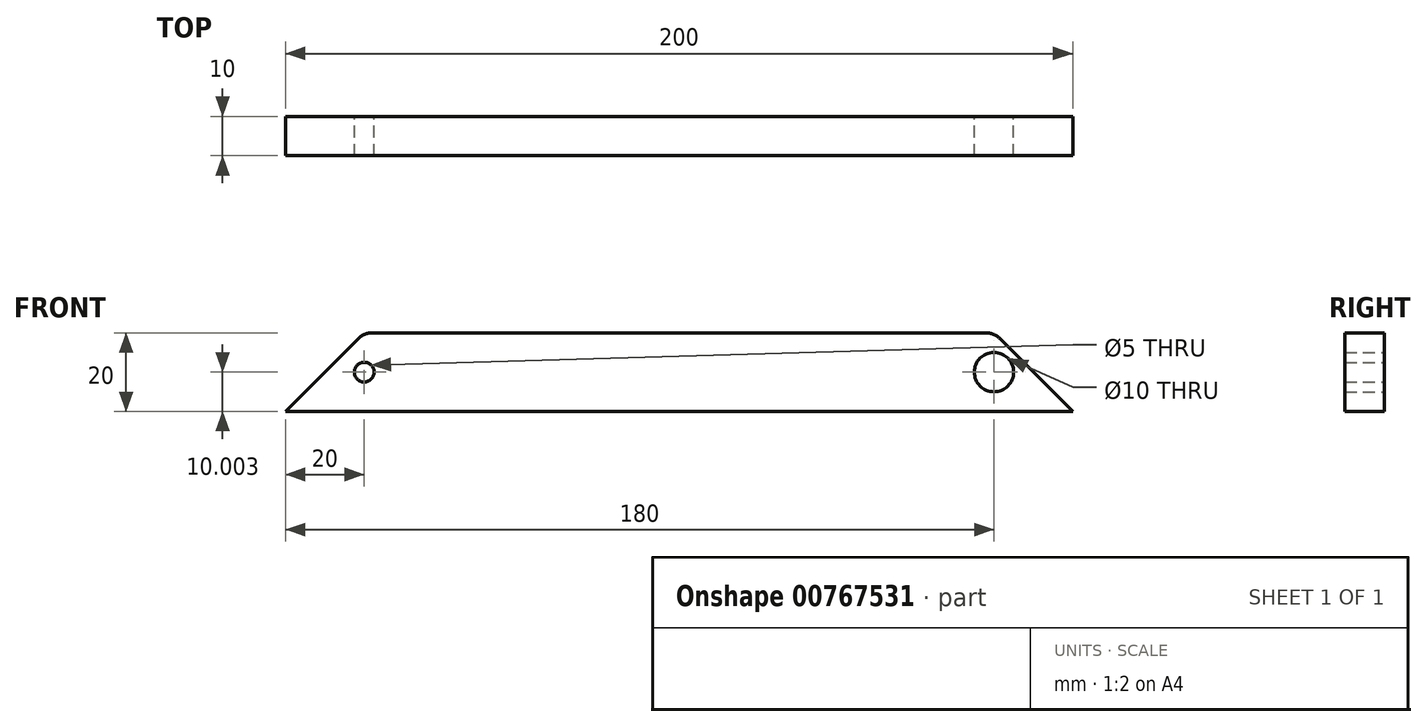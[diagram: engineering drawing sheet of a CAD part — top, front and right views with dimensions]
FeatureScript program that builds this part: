
annotation { "Feature Type Name" : "Feature", "Feature Type Description" : "" }
export const myFeature = defineFeature(function(context is Context, id is Id, definition is map)
    precondition{}
    {
        {
            var Q0;
            Q0=qCreatedBy(makeId("Front.planeOp"),FACE);
            var sketch = newSketch(context, id + "F0", { "sketchPlane" : qUnion([Q0])});
            skLineSegment(sketch, "E0.bottom", {"start": v(-75, -3.38) * mm, "end": v(125, -3.38) * mm});
            skLineSegment(sketch, "E0.top", {"start": v(-75, -23.38) * mm, "end": v(125, -23.38) * mm});
            skLineSegment(sketch, "E0.left", {"start": v(-75, -3.38) * mm, "end": v(-75, -23.38) * mm});
            skLineSegment(sketch, "E0.right", {"start": v(125, -3.38) * mm, "end": v(125, -23.38) * mm});
            skPoint(sketch, "E1", {"position": v(-55, -13.38) * mm});
            skPoint(sketch, "E2", {"position": v(105, -13.38) * mm});
            skCircle(sketch, "E3", {"center": v(-55, -13.38) * mm, "radius": 2.5 * mm});
            skCircle(sketch, "E4", {"center": v(105, -13.38) * mm, "radius": 5 * mm});
            skSolve(sketch);
        }
        {
            var Q0;
            Q0=makeQuery(id+"F0.imprint","IMPRINT",FACE,{"disambiguationData":[TD([[makeQuery(id+"F0.imprint","IMPRINT",EDGE,{"derivedFrom":sQuery(id+"F0.wireOp",EDGE,"E0.bottom")}),-1.0]])]});
            extrude(context, id + "F1", {"entities" : qUnion([Q0]), "endBound" : BoundingType.SYMMETRIC, "depth" : 10 * mm, "offsetDistance" : 25 * mm});
        }
        {
            var Q0;
            Q0=makeQuery(id+"F1.opExtrude","SWEPT_EDGE",EDGE,{"disambiguationData":[OSD([sQuery(id+"F0.wireOp",EDGE,"E0.bottom"),sQuery(id+"F0.wireOp",EDGE,"E0.left")])]});
            var Q1;
            Q1=makeQuery(id+"F1.opExtrude","SWEPT_EDGE",EDGE,{"disambiguationData":[OSD([sQuery(id+"F0.wireOp",EDGE,"E0.bottom"),sQuery(id+"F0.wireOp",EDGE,"E0.right")])]});
            chamfer(context, id + "F2", {"entities" : qUnion([Q0, Q1]), "width" : 20 * mm, "tangentPropagation" : true});
        }
        {
            var Q0;
            {var subQ0=sQuery(id+"F0.wireOp",EDGE,"E0.bottom");Q0=makeQuery(id+"F2.opChamfer","BLEND_EDGE",EDGE,{"blendedFrom":[makeQuery(id+"F1.opExtrude","SWEPT_EDGE",EDGE,{"disambiguationData":[OSD([subQ0,sQuery(id+"F0.wireOp",EDGE,"E0.left")])]}),makeQuery(id+"F1.opExtrude","SWEPT_FACE",FACE,{"disambiguationData":[OSD([subQ0])]})],"blendedInto":[makeQuery(id+"F1.opExtrude","SWEPT_FACE",FACE,{"disambiguationData":[OSD([subQ0])]})]});}
            var Q1;
            {var subQ0=sQuery(id+"F0.wireOp",EDGE,"E0.bottom");Q1=makeQuery(id+"F2.opChamfer","BLEND_EDGE",EDGE,{"blendedFrom":[makeQuery(id+"F1.opExtrude","SWEPT_EDGE",EDGE,{"disambiguationData":[OSD([subQ0,sQuery(id+"F0.wireOp",EDGE,"E0.right")])]}),makeQuery(id+"F1.opExtrude","SWEPT_FACE",FACE,{"disambiguationData":[OSD([subQ0])]})],"blendedInto":[makeQuery(id+"F1.opExtrude","SWEPT_FACE",FACE,{"disambiguationData":[OSD([subQ0])]})]});}
            fillet(context, id + "F3", {"entities" : qUnion([Q0, Q1]), "radius" : 5 * mm, "tangentPropagation" : true, "allowEdgeOverflow" : false});
        }
    });
